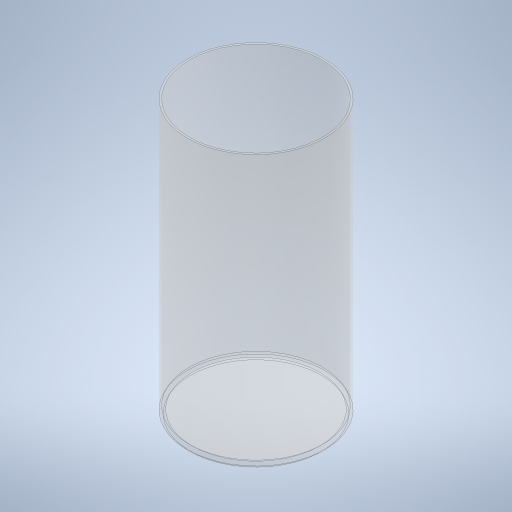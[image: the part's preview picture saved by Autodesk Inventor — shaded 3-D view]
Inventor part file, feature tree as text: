
AUTODESK INVENTOR PART (.ipt)
format: ipt  version: 2024 (Build 280153000, 153)  size: 280,064 bytes
history: native  units: mm
features: extrude x2, sketch x1, fillet x1
ambient origin geometry x8: Origin, YZ Plane, XZ Plane, XY Plane, X Axis, Y Axis, Z Axis, Center Point
bodies: Solide1 (feature_tree)
feature tree (4):
  sketch  "Esquisse1"
  extrude  "Extrusion1"  Depth=90.61mm
  extrude  "Extrusion2"  Depth=93.19mm
  fillet  "Congé1"  Radius=185.0mm
